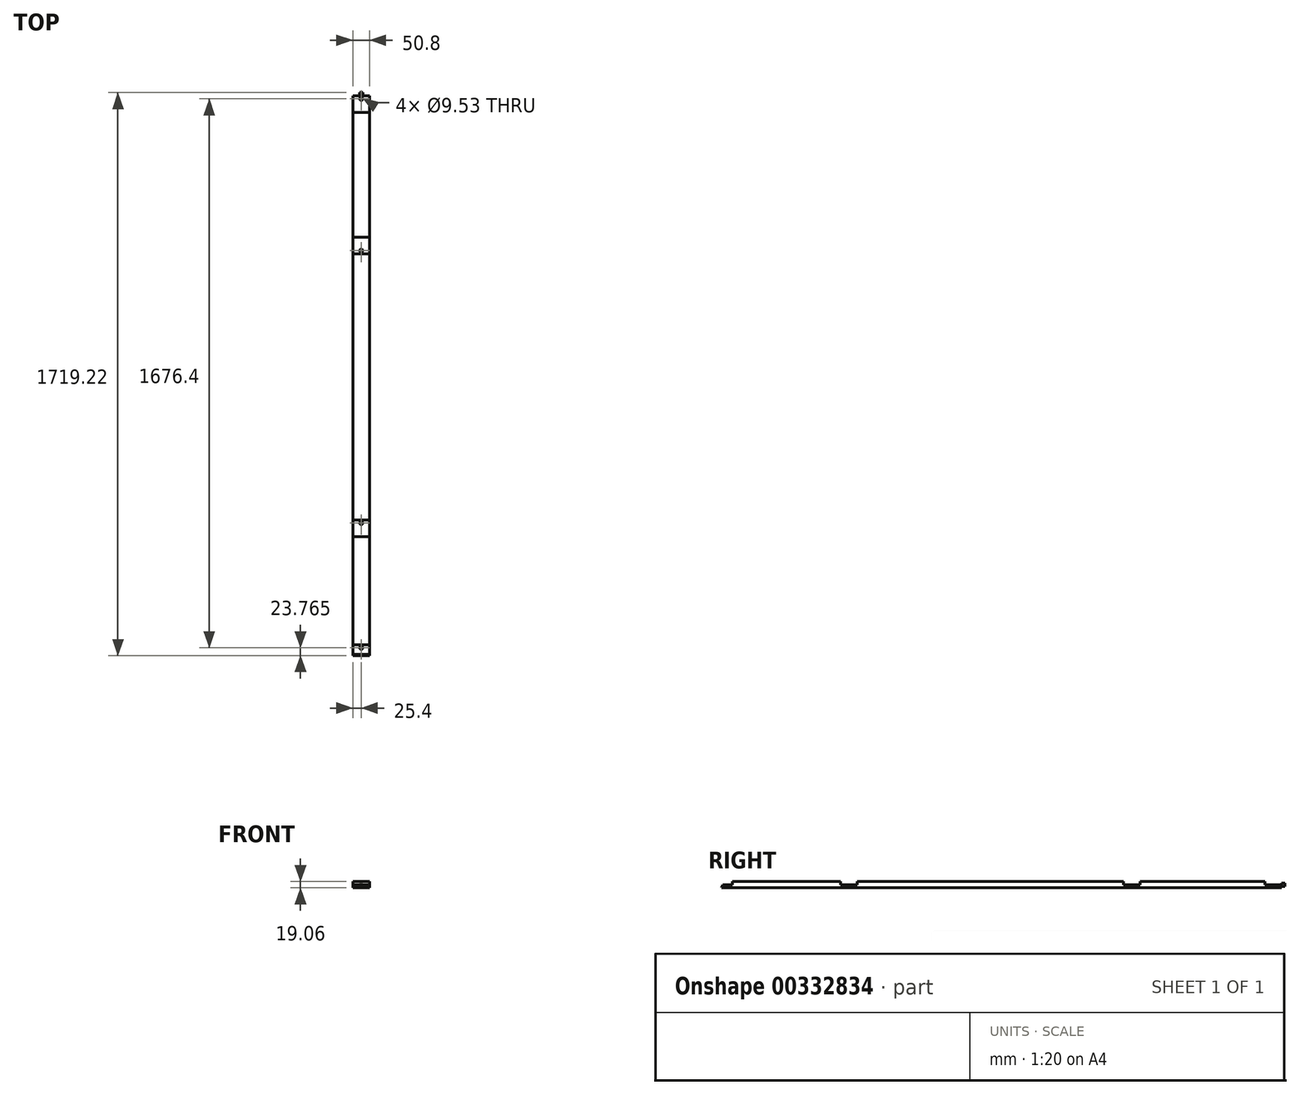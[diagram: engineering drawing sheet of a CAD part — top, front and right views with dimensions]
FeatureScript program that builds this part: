
annotation { "Feature Type Name" : "Feature", "Feature Type Description" : "" }
export const myFeature = defineFeature(function(context is Context, id is Id, definition is map)
    precondition{}
    {
        {
            var Q0;
            Q0=qCreatedBy(makeId("Right.planeOp"),FACE);
            var sketch = newSketch(context, id + "F0", { "sketchPlane" : qUnion([Q0])});
            skLineSegment(sketch, "E0.top", {"start": v(1676.4, -9.52) * mm, "end": v(1676.4, 0) * mm});
            skLineSegment(sketch, "E0.right", {"start": v(0, 9.52) * mm, "end": v(330.2, 9.53) * mm});
            skLineSegment(sketch, "E1.top", {"start": v(0, 9.52) * mm, "end": v(0, 0) * mm});
            skLineSegment(sketch, "E1.right", {"start": v(-29.35, 0) * mm, "end": v(0, 0) * mm});
            skLineSegment(sketch, "E2.top", {"start": v(1625.6, 9.53) * mm, "end": v(1625.6, 0) * mm});
            skLineSegment(sketch, "E2.right", {"start": v(1676.4, 0) * mm, "end": v(1625.6, 0) * mm});
            skLineSegment(sketch, "E3", {"start": v(-25.4, 9.52) * mm, "end": v(-33.3, -9.53) * mm});
            skLineSegment(sketch, "E4", {"start": v(1676.4, -9.52) * mm, "end": v(-33.3, -9.53) * mm});
            skLineSegment(sketch, "E5.right", {"start": v(1625.6, 0) * mm, "end": v(1625.6, 0) * mm});
            skLineSegment(sketch, "E6.trimOffspring", {"start": v(1625.6, 9.53) * mm, "end": v(1625.6, 9.53) * mm});
            skLineSegment(sketch, "E7.top", {"start": v(1193.8, 9.53) * mm, "end": v(1193.8, 0) * mm});
            skLineSegment(sketch, "E7.right", {"start": v(1244.6, 0) * mm, "end": v(1193.8, 0) * mm});
            skLineSegment(sketch, "E8.bottom", {"start": v(381, 9.53) * mm, "end": v(381, 0) * mm});
            skLineSegment(sketch, "E8.top", {"start": v(330.2, 9.53) * mm, "end": v(330.2, 0) * mm});
            skLineSegment(sketch, "E8.right", {"start": v(381, 0) * mm, "end": v(330.2, 0) * mm});
            skPoint(sketch, "E8.left.start.orphan", {"position": v(381, 48.5) * mm});
            skPoint(sketch, "E9.orphan", {"position": v(330.2, 48.5) * mm});
            skLineSegment(sketch, "E10.trimOffspring", {"start": v(381, 9.53) * mm, "end": v(1193.8, 9.53) * mm});
            skLineSegment(sketch, "E11", {"start": v(1244.6, 0) * mm, "end": v(1244.6, 9.53) * mm});
            skLineSegment(sketch, "E12.trimOffspring", {"start": v(1244.6, 9.53) * mm, "end": v(1625.6, 9.53) * mm});
            skLineSegment(sketch, "E13", {"start": v(0, 9.52) * mm, "end": v(-25.4, 9.52) * mm, "construction": true});
            skSolve(sketch);
        }
        {
            var Q0;
            Q0 = qSketchRegion(id + "F0", true);
            extrude(context, id + "F1", {"entities" : qUnion([Q0]), "endBound" : BoundingType.SYMMETRIC, "depth" : 50.8 * mm});
        }
        {
            var Q0;
            Q0=qCreatedBy(makeId("Front.planeOp"),FACE);
            cPlane(context, id + "F2", {"entities" : qUnion([Q0]), "cplaneType" : CPlaneType.OFFSET, "offset" : 1676.4 * mm, "oppositeDirection" : true, "width" : 152.4 * mm, "height" : 152.4 * mm});
        }
        {
            var Q0;
            Q0=qCreatedBy(id+"F2.planeOp",FACE);
            var sketch = newSketch(context, id + "F3", { "sketchPlane" : qUnion([Q0])});
            skCircle(sketch, "E14", {"center": v(0, 0) * mm, "radius": 4.76 * mm});
            skSolve(sketch);
        }
        {
            var Q0;
            Q0 = qSketchRegion(id + "F3", true);
            extrude(context, id + "F4", {"entities" : qUnion([Q0]), "operationType" : NewBodyOperationType.ADD, "oppositeDirection" : true, "depth" : 9.52 * mm});
        }
        {
            var Q0;
            Q0=qCreatedBy(makeId("Top.planeOp"),FACE);
            var sketch = newSketch(context, id + "F5", { "sketchPlane" : qUnion([Q0])});
            skCircle(sketch, "E15", {"center": v(0, 371.48) * mm, "radius": 4.76 * mm});
            skCircle(sketch, "E16", {"center": v(0, 1203.33) * mm, "radius": 4.76 * mm});
            skCircle(sketch, "E17", {"center": v(0, 1666.88) * mm, "radius": 4.76 * mm});
            skCircle(sketch, "E18", {"center": v(0, -9.52) * mm, "radius": 4.76 * mm});
            skSolve(sketch);
        }
        {
            var Q0;
            Q0 = qSketchRegion(id + "F5", true);
            extrude(context, id + "F6", {"entities" : qUnion([Q0]), "operationType" : NewBodyOperationType.REMOVE, "oppositeDirection" : true, "depth" : 25.4 * mm});
        }
    });
